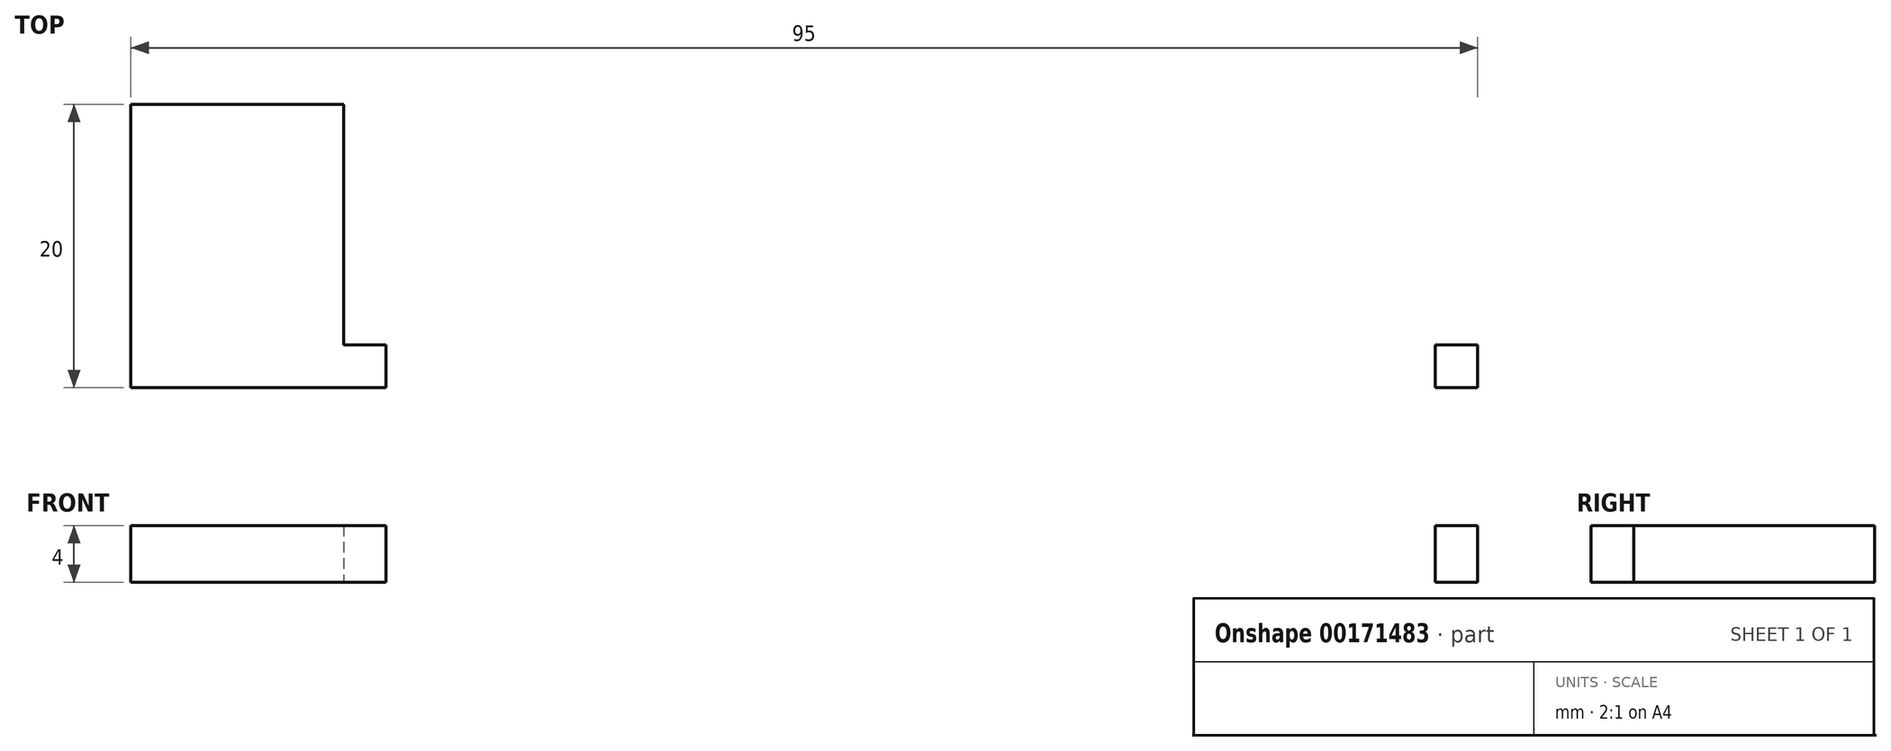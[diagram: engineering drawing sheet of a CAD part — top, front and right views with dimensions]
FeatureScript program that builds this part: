
annotation { "Feature Type Name" : "Feature", "Feature Type Description" : "" }
export const myFeature = defineFeature(function(context is Context, id is Id, definition is map)
    precondition{}
    {
        {
            var Q0;
            Q0=qCreatedBy(makeId("Top.planeOp"),FACE);
            var sketch = newSketch(context, id + "F0", { "sketchPlane" : qUnion([Q0])});
            skLineSegment(sketch, "E0.bottom", {"start": v(-40, -32) * mm, "end": v(40, -32) * mm});
            skLineSegment(sketch, "E0.top", {"start": v(-40, 32) * mm, "end": v(40, 32) * mm});
            skLineSegment(sketch, "E0.left", {"start": v(-40, -32) * mm, "end": v(-40, 32) * mm});
            skLineSegment(sketch, "E0.right", {"start": v(40, -32) * mm, "end": v(40, 32) * mm});
            skPoint(sketch, "E0.middle", {"position": v(0, 0) * mm});
            skLineSegment(sketch, "E1.bottom", {"start": v(-40, -32) * mm, "end": v(-55, -32) * mm});
            skLineSegment(sketch, "E1.top", {"start": v(-40, -12) * mm, "end": v(-55, -12) * mm});
            skLineSegment(sketch, "E1.left", {"start": v(-40, -32) * mm, "end": v(-40, -12) * mm});
            skLineSegment(sketch, "E1.right", {"start": v(-55, -32) * mm, "end": v(-55, -12) * mm});
            skLineSegment(sketch, "E2.bottom", {"start": v(40, -32) * mm, "end": v(37, -32) * mm});
            skLineSegment(sketch, "E2.top", {"start": v(40, -29) * mm, "end": v(37, -29) * mm});
            skLineSegment(sketch, "E2.left", {"start": v(40, -32) * mm, "end": v(40, -29) * mm});
            skLineSegment(sketch, "E2.right", {"start": v(37, -32) * mm, "end": v(37, -29) * mm});
            skLineSegment(sketch, "E3.bottom", {"start": v(-40, -32) * mm, "end": v(-37, -32) * mm});
            skLineSegment(sketch, "E3.top", {"start": v(-40, -29) * mm, "end": v(-37, -29) * mm});
            skLineSegment(sketch, "E3.left", {"start": v(-40, -32) * mm, "end": v(-40, -29) * mm});
            skLineSegment(sketch, "E3.right", {"start": v(-37, -32) * mm, "end": v(-37, -29) * mm});
            skLineSegment(sketch, "E4.bottom", {"start": v(0, 32) * mm, "end": v(3, 32) * mm});
            skLineSegment(sketch, "E4.top", {"start": v(0, 29) * mm, "end": v(3, 29) * mm});
            skLineSegment(sketch, "E4.left", {"start": v(0, 32) * mm, "end": v(0, 29) * mm});
            skLineSegment(sketch, "E4.right", {"start": v(3, 32) * mm, "end": v(3, 29) * mm});
            skSolve(sketch);
        }
        {
            var Q0;
            Q0=makeQuery(id+"F0.imprint","IMPRINT",FACE,{"disambiguationData":[TD([[makeQuery(id+"F0.imprint","IMPRINT",EDGE,{"derivedFrom":sQuery(id+"F0.wireOp",EDGE,"E1.bottom")}),-1.0]])]});
            var Q1;
            Q1=makeQuery(id+"F0.imprint","IMPRINT",FACE,{"disambiguationData":[TD([[makeQuery(id+"F0.imprint","IMPRINT",EDGE,{"derivedFrom":sQuery(id+"F0.wireOp",EDGE,"E0.bottom")}),1.0]])]});
            extrude(context, id + "F1", {"entities" : qUnion([Q0, Q1]), "depth" : 4 * mm});
        }
    });
